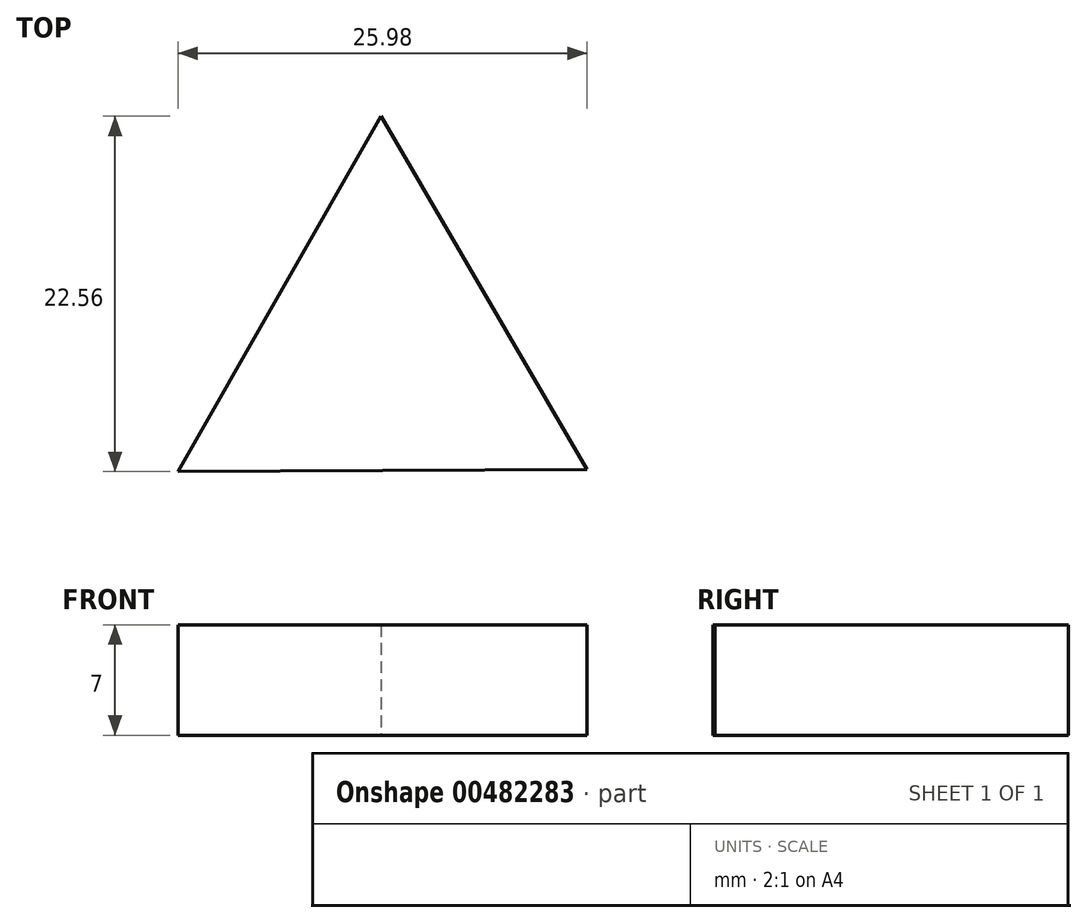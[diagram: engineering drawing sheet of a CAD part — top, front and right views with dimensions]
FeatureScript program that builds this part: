
annotation { "Feature Type Name" : "Feature", "Feature Type Description" : "" }
export const myFeature = defineFeature(function(context is Context, id is Id, definition is map)
    precondition{}
    {
        {
            var Q0;
            Q0=qCreatedBy(makeId("Top.planeOp"),FACE);
            var sketch = newSketch(context, id + "F0", { "sketchPlane" : qUnion([Q0])});
            skCircle(sketch, "E0.cCircle", {"center": v(0, 0) * mm, "radius": 15 * mm, "construction": true});
            skLineSegment(sketch, "E0.0", {"start": v(13.02, -7.44) * mm, "end": v(-12.96, -7.56) * mm});
            skLineSegment(sketch, "E0.1", {"start": v(-12.96, -7.56) * mm, "end": v(-0.07, 15) * mm});
            skLineSegment(sketch, "E0.2", {"start": v(-0.07, 15) * mm, "end": v(13.02, -7.44) * mm});
            skSolve(sketch);
        }
        {
            var Q0;
            Q0=makeQuery(id+"F0.imprint","IMPRINT",FACE,{"disambiguationData":[TD([[makeQuery(id+"F0.imprint","IMPRINT",EDGE,{"derivedFrom":sQuery(id+"F0.wireOp",EDGE,"E0.0")}),-1.0]])]});
            extrude(context, id + "F1", {"entities" : qUnion([Q0]), "depth" : 7 * mm});
        }
    });
